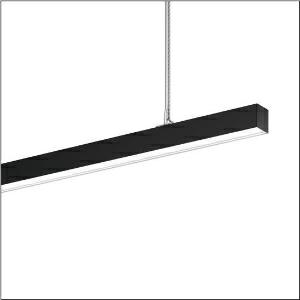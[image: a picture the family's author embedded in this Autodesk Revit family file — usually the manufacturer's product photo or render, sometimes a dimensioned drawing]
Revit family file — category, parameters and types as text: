
# Revit family: silica_r__21_51mx33tctdb_eeca
name_source: partatom
category: Lighting Fixtures
units: mm (PartAtom-declared; Revit-internal decimal feet)

## family parameters
Cut with Voids When Loaded = No
Host = Face
Light Source = No
Part Type = Normal
Room Calculation Point = No
Round Connector Dimension = Use Diameter
Shared = No

## types (1)
- --- (1 x LED, 14340 lm, 134.7 W, 6500K)
    Apparent Load = 135 VA
    CIE Flux Codes = 78 96 99 56 100
    Color Rendering = 80
    Color Temperature = 6500K
    Default Elevation = 1800 mm
    Description = Silica® 21, office luminaire, primary optical cover: prismatic diffuser, of PMMA, CAT 2 (L<= 3000cd/m²), light emission: direct/indirect distribution, primary light characteristic: symmetric, installation type: suspended mounting, LED, rated luminous flux: 14.340lm, luminous efficacy: 101lm/W, light colour: 8tw, colour temperature: 2700..6500K, control gear: ECG DALI, with terminal, 3+2-pole, max. 2.5mm², mains connection: 220..240V, AC, 50/60Hz, rated input power: 141.4W, luminaire housing, of aluminium, jet black (RAL 9005), length: 3.004mm, width: 53mm, height: 53mm, protection rating (complete): IP20, insulation class (complete): insulation class I (protective earthing), certification: CE, permissible operating ambient temperature: 0..+35°C, standard: EN 50419, packaging unit: 1 piece
    Height = 53 mm
    Lamp = 1 x LED
    Lamp Light Flux = 14340 lm
    Lamp Power = 134.7 W
    Lamp count = 1
    Length = 3004 mm
    Luminous efficacy = 106 lm/W
    Manufacturer = Siteco
    ModVariant = No
    Model = 51MX33TCTDB
    Mounting Place = Ceiling
    Mounting Type = Pendant
    Number of Poles = 1
    OnlyDefault = Yes
    Power Factor = 1
    Product Name = Silica® 21
    Product group = office luminaire | ceiling pendant
    ProductGroupID = 902
    Protection Class = Protection class I
    Protection Degree = IP 20
    RLX_Detail_Level = 1
    RLX_Emergency_Light_Flux = 0 lm
    RLX_Emergency_Type = 0
    RLX_Emergency_Type_DB = No
    RlxData = <blob elided: 22853 chars, md5=730bd5d7>
    Socket = socket
    Standby Power = 0 W
    System Light Flux = 14340 lm
    System Power = 135 W
    Type Comments = individual setting
    Type Image = l_1313646.jpg
    URL = http://relux.com
    VarID = @adj_089121
    Voltage = 0 V
    Weight = 0.00 kg
    Width = 53 mm

## geometry (parser evidence)
native form markers: Blend x4, Sweep x12
no freeform markers — native parametric forms only
